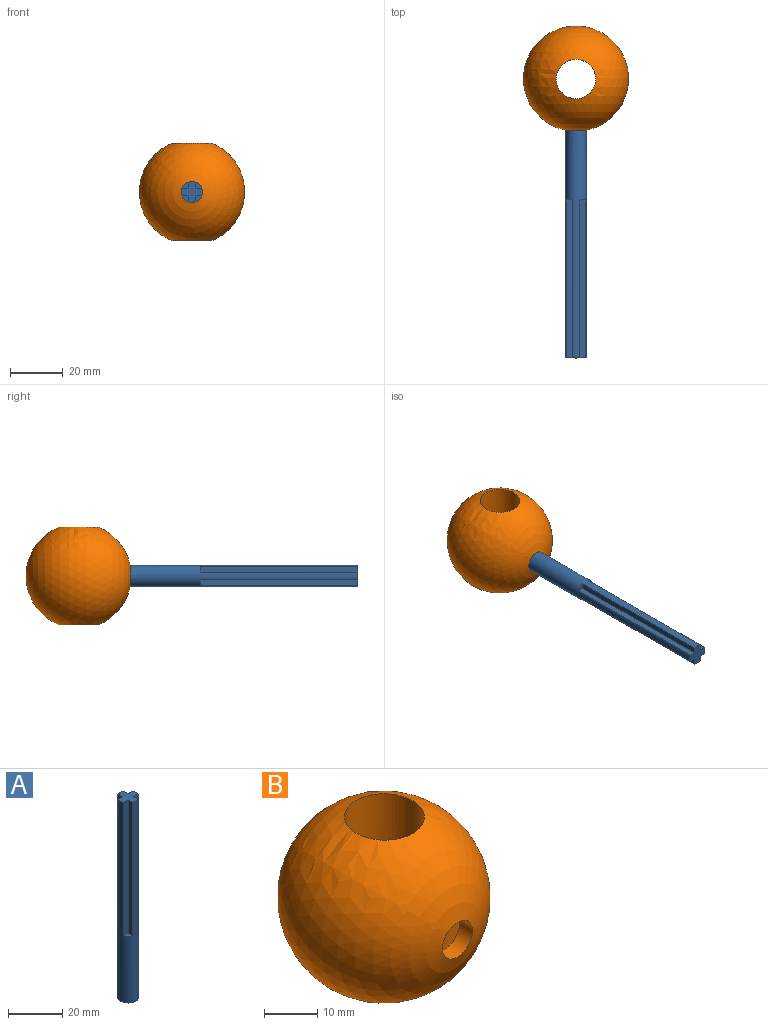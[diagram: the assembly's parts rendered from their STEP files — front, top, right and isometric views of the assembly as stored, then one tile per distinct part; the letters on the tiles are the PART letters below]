
ASSEMBLY  parts=2 mates=1
PART A: 15 faces, bbox 8x8x90 mm
  f0: plane 2.21x2.21mm, normal (0,0,1), area 3.1mm2, adj f4,f10,f11
  f1: plane 2.21x2.21mm, normal (0,0,1), area 3.1mm2, adj f4,f8,f9
  f2: plane 2.21x2.21mm, normal (0,0,1), area 3.1mm2, adj f4,f6,f7
  f3: plane 2.21x2.21mm, normal (0,0,1), area 3.1mm2, adj f4,f12,f13
  f4: cylinder r=4mm len=90mm, axis (0,0,1), area 1492mm2, adj f0,f1,f2,f3,f5,f6,f7,f8
  f5: plane 8x8mm, normal (0,0,-1), area 50.3mm2, adj f4
  f6: plane 60x2.21mm, normal (-1,0,0), area 132.5mm2, adj f2,f4,f7,f14
  f7: plane 60x2.21mm, normal (0,1,0), area 132.5mm2, adj f2,f4,f6,f14
  f8: plane 60x2.21mm, normal (0,-1,0), area 132.5mm2, adj f1,f4,f9,f14
  f9: plane 60x2.21mm, normal (-1,0,0), area 132.5mm2, adj f1,f4,f8,f14
  f10: plane 60x2.21mm, normal (1,0,0), area 132.5mm2, adj f0,f4,f11,f14
  f11: plane 60x2.21mm, normal (0,-1,0), area 132.5mm2, adj f0,f4,f10,f14
  f12: plane 60x2.21mm, normal (0,1,0), area 132.5mm2, adj f3,f4,f13,f14
  f13: plane 60x2.21mm, normal (1,0,0), area 132.5mm2, adj f3,f4,f12,f14
  f14: plane 8x8mm, normal (0,0,1), area 37.8mm2, adj f4,f6,f7,f8,f9,f10,f11,f12
PART B: 4 faces, bbox 40x39.6x40 mm
  f0: sphere r=20mm, area 4608.8mm2, adj f1,f2
  f1: cylinder r=7.5mm len=37.2mm, axis (0,0,1), area 1747.3mm2, adj f0
  f2: cylinder r=4mm len=8mm, axis (0,-1,0), area 88.2mm2, adj f0,f3
  f3: plane 8x8mm, normal (0,-1,0), area 50.3mm2, adj f2
PLACE A rot(axis=(1,0,0),90deg) t=(-14.68,9.57,12.47)mm
PLACE B t=(0.14,-37.69,12.47)mm
MATE fastened A.f4 <-> B.f2  axis (0,1,0) through (0.14,-7.69,12.47)mm
